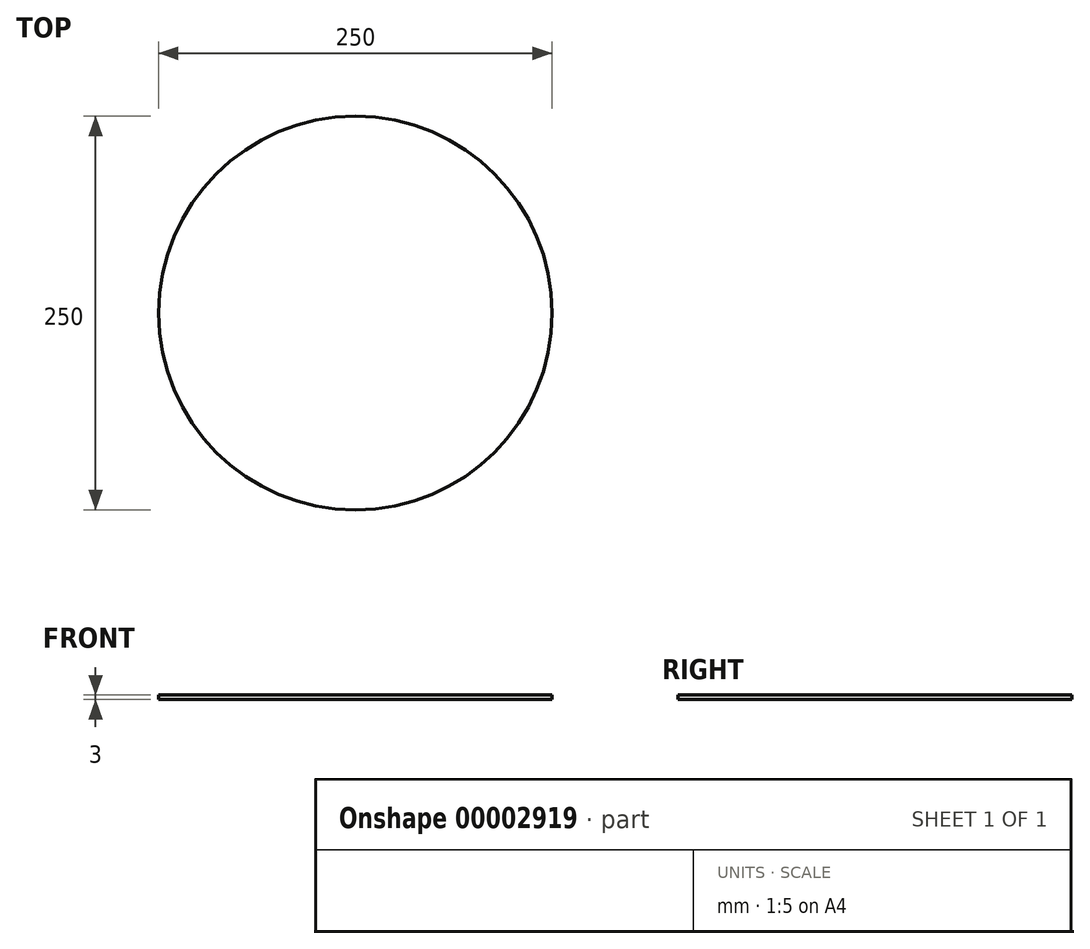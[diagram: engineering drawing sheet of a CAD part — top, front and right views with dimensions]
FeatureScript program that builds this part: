
annotation { "Feature Type Name" : "Feature", "Feature Type Description" : "" }
export const myFeature = defineFeature(function(context is Context, id is Id, definition is map)
    precondition{}
    {
        {
            var Q0;
            Q0=qCreatedBy(makeId("Top.planeOp"),FACE);
            var sketch = newSketch(context, id + "F0", { "sketchPlane" : qUnion([Q0])});
            skCircle(sketch, "E0", {"center": v(0, 0) * mm, "radius": 125 * mm});
            skSolve(sketch);
        }
        {
            var Q0;
            Q0=makeQuery(id+"F0.imprint","IMPRINT",FACE,{"disambiguationData":[TD([[makeQuery(id+"F0.imprint","IMPRINT",EDGE,{"derivedFrom":sQuery(id+"F0.wireOp",EDGE,"E0")}),1.0]])]});
            extrude(context, id + "F1", {"entities" : qUnion([Q0]), "depth" : 3 * mm});
        }
    });
